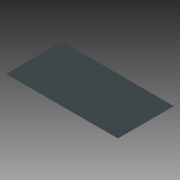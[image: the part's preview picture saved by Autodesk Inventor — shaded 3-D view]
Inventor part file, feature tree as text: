
AUTODESK INVENTOR PART (.ipt)
format: ipt  version: 2012 (Build 160160000, 160)  size: 67,584 bytes
history: native  units: in
note: dims shown in document units (in); Inventor stores cm internally (conversion verified against a paired STEP export)
features: extrude x1, sketch x1
ambient origin geometry x8: Origin, YZ Plane, XZ Plane, XY Plane, X Axis, Y Axis, Z Axis, Center Point
bodies: Solid1 (feature_tree)
feature tree (2):
  extrude  "Extrusion1"  Depth=648.0in
  sketch  "Sketch1"  dims[d0=0.5in d1=648.0in d2=324.0in d3=0.0in]
